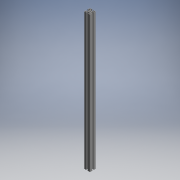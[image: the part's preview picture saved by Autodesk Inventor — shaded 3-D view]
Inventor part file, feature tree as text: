
AUTODESK INVENTOR PART (.ipt)
format: ipt  version: 2017.3 (Build 213256000, 256)  size: 210,432 bytes
history: native  units: mm (DEFAULTED — no unit token found)
features: other x21, sketch x3, hole x2, extrude x1, pattern_linear x1
ambient origin geometry x8: Origin, YZ Plane, XZ Plane, XY Plane, X Axis, Y Axis, Z Axis, Center Point
bodies: Solid1 (feature_tree)
feature tree (28):
  extrude  "Extrusion1"  Depth=690.0mm
  hole  "Hole1"  [1 undecoded]
  hole  "Hole2"  [1 undecoded]
  pattern_linear  "Rectangular Pattern1"  [2 undecoded]
  other  "C1_XY"
  other  "C1_YZ"
  other  "C1_ZX"
  other  "C1_X"
  other  "C1_Y"
  other  "C1_Z"
  other  "C1_Center"
  other  "to_frame_cap1_XY"
  other  "to_frame_cap1_YZ"
  other  "to_frame_cap1_ZX"
  other  "to_frame_cap1_X"
  other  "to_frame_cap1_Y"
  other  "to_frame_cap1_Z"
  other  "to_frame_cap1_Center"
  other  "to_frame_cap2_XY"
  other  "to_frame_cap2_YZ"
  other  "to_frame_cap2_ZX"
  other  "to_frame_cap2_X"
  other  "to_frame_cap2_Y"
  other  "to_frame_cap2_Z"
  other  "to_frame_cap2_Center"
  sketch  "Sketch_1"  dims[d0=690.0mm d1=0.0mm]
  sketch  "Sketch2"  dims[d2=6.8mm d3=6.0mm d4=4.0mm d5=2.0mm d6=90.0deg d7=690.0mm d8=0.0mm]
  sketch  "Sketch3"  dims[d9=4.2mm d10=6.0mm d11=4.0mm d12=2.0mm d13=90.0deg d14=690.0mm d15=0.0mm d16=20.0mm d18=23.2mm d19=20.0mm d21=23.2mm d22=0.0mm d23=0.0mm d24=0.0mm]
note: 4 required parameter values undecoded (feature->parameter linkage not recoverable at this tier; creation-order binding heuristic only, values carry confidence <= 0.55)
